FCSTD DOCUMENT  (FreeCAD 0.19R24276 (Git))
Label: pir-baffel-assembly
License: All rights reserved
LicenseURL: http://en.wikipedia.org/wiki/All_rights_reserved
objects: TechDraw::DrawViewDimension×10, App::Link×7, TechDraw::DrawViewAnnotation×5, TechDraw::DrawViewPart×4, App::DocumentObjectGroup×3, TechDraw::DrawHatch×3, PartDesign::CoordinateSystem×1, App::FeaturePython×1, App::Part×1, TechDraw::DrawSVGTemplate×1, TechDraw::DrawPage×1
note: 1 computed .brp shape members not serialized (recipe doc carries the construction recipe); baked Part::Feature solids carry a one-line shape summary decoded from their .brp
EXTERNAL_REF file=pir-baffel-top.FCStd obj=LCS_top
EXTERNAL_REF file=pir-baffel-top.FCStd obj=Body
EXTERNAL_REF file=pir-baffel-side.FCStd obj=LCS_side
EXTERNAL_REF file=pir-baffel-side.FCStd obj=Body
EXTERNAL_REF file=pir-baffel-bottomFront.FCStd obj=LCS_bottomFront
EXTERNAL_REF file=pir-baffel-bottomFront.FCStd obj=Body
EXTERNAL_REF file=pir-baffel-bottomBack.FCStd obj=LCS_bottomBack
EXTERNAL_REF file=pir-baffel-bottomBack.FCStd obj=Body
EXTERNAL_REF file=pir-baffel-screwBlock-assembly.FCStd obj=LCS_Origin
EXTERNAL_REF file=pir-baffel-screwBlock-assembly.FCStd obj=Model

FEATURE [App::DocumentObjectGroup] Parts
FEATURE [PartDesign::CoordinateSystem] LCS_Origin
  AttacherType = Attacher::AttachEngine3D
  MapMode = 2
  Support = -> [X_Axis]
FEATURE [App::DocumentObjectGroup] Constraints
FEATURE [App::FeaturePython] Variables  # WARN: FeaturePython — macro-defined, semantics opaque (R4)
FEATURE [App::Link] pir_baffel_top_Body
  AssemblyType = Asm4EE
  AttachedBy = #LCS_top
  AttachedTo = Parent Assembly#LCS_Origin
  LinkPlacement = pos=(0,0,-0.8) rot=(0,0,-1;1.5708rad)
  LinkedObject = -> <external pir-baffel-top.FCStd>#Body
  Placement = pos=(0,0,-0.8) rot=(0,0,-1;1.5708rad)
  expr: Placement = LCS_Origin.Placement * AttachmentOffset * pir_baffel_top#LCS_top.Placement ^ -1
FEATURE [App::Link] pir_baffel_side_left_Body
  AssemblyType = Asm4EE
  AttachedBy = #LCS_side
  AttachedTo = pir_baffel_top_Body#LCS_top
  AttachmentOffset = pos=(29,0,-26.6) rot=(0,1,0;4.71239rad)
  LinkPlacement = pos=(30.5785,9e-16,-25.8272) rot=(-0.576884,0.576884,0.578283;4.19019rad)
  LinkedObject = -> <external pir-baffel-side.FCStd>#Body
  Placement = pos=(30.5785,9e-16,-25.8272) rot=(-0.576884,0.576884,0.578283;4.19019rad)
  expr: Placement = pir_baffel_top_Body.Placement * pir_baffel_top#LCS_top.Placement * AttachmentOffset * pir_baffel_side#LCS_side.Placement ^ -1
FEATURE [App::Link] pir_baffel_side_right_Body
  AssemblyType = Asm4EE
  AttachedBy = #LCS_side
  AttachedTo = pir_baffel_top_Body#LCS_top
  AttachmentOffset = pos=(-29.1,0,-25) rot=(0,-1,0;4.71239rad)
  LinkPlacement = pos=(-30.6785,2e-16,-25.7728) rot=(0.577816,-0.577816,0.576418;4.18739rad)
  LinkedObject = -> <external pir-baffel-side.FCStd>#Body
  Placement = pos=(-30.6785,2e-16,-25.7728) rot=(0.577816,-0.577816,0.576418;4.18739rad)
  expr: Placement = pir_baffel_top_Body.Placement * pir_baffel_top#LCS_top.Placement * AttachmentOffset * pir_baffel_side#LCS_side.Placement ^ -1
FEATURE [App::Link] pir_baffel_bottomFront_Body
  AssemblyType = Asm4EE
  AttachedBy = #LCS_bottomFront
  AttachedTo = pir_baffel_top_Body#LCS_top
  AttachmentOffset = pos=(29,-30.7,-51.6) rot=(0.707107,0,0.707107;3.14159rad)
  LinkPlacement = pos=(7.1e-15,-30.7,-52.4) rot=(0,0,1;4.71239rad)
  LinkedObject = -> <external pir-baffel-bottomFront.FCStd>#Body
  Placement = pos=(7.1e-15,-30.7,-52.4) rot=(0,0,1;4.71239rad)
  expr: Placement = pir_baffel_top_Body.Placement * pir_baffel_top#LCS_top.Placement * AttachmentOffset * pir_baffel_bottomFront#LCS_bottomFront.Placement ^ -1
FEATURE [App::DocumentObjectGroup] Measures
FEATURE [App::Link] pir_baffel_bottomBack_Body
  AssemblyType = Asm4EE
  AttachedBy = #LCS_bottomBack
  AttachedTo = pir_baffel_top_Body#LCS_top
  AttachmentOffset = pos=(0,40,-54.1) rot=(0.707107,-0.707107,0;3.14159rad)
  LinkPlacement = pos=(-1e-16,40,-52.5) rot=(1,0,0;3.14159rad)
  LinkedObject = -> <external pir-baffel-bottomBack.FCStd>#Body
  Placement = pos=(-1e-16,40,-52.5) rot=(1,0,0;3.14159rad)
  expr: Placement = pir_baffel_top_Body.Placement * pir_baffel_top#LCS_top.Placement * AttachmentOffset * pir_baffel_bottomBack#LCS_bottomBack.Placement ^ -1
FEATURE [App::Link] pir_baffel_screwBlock1_assembly
  AssemblyType = Asm4EE
  AttachedBy = #LCS_Origin
  AttachedTo = pir_baffel_side_left_Body#LCS_side
  AttachmentOffset = pos=(-18.2,40,-4.8) rot=(0,0,1;0rad)
  LinkPlacement = pos=(33.8,40,-44.8) rot=(0,1,0;4.71239rad)
  LinkedObject = -> <external pir-baffel-screwBlock-assembly.FCStd>#Model
  Placement = pos=(33.8,40,-44.8) rot=(0,1,0;4.71239rad)
  expr: Placement = pir_baffel_side_left_Body.Placement * pir_baffel_side#LCS_side.Placement * AttachmentOffset * pir_baffel_screwBlock_assembly#LCS_Origin.Placement ^ -1
FEATURE [App::Link] pir_baffel_screwBlock2_assembly
  AssemblyType = Asm4EE
  AttachedBy = #LCS_Origin
  AttachedTo = pir_baffel_side_right_Body#LCS_side
  AttachmentOffset = pos=(20,39.8,-4.8) rot=(0,0,1;0rad)
  LinkPlacement = pos=(-33.9,39.8,-45) rot=(0,-1,0;4.71239rad)
  LinkedObject = -> <external pir-baffel-screwBlock-assembly.FCStd>#Model
  Placement = pos=(-33.9,39.8,-45) rot=(0,-1,0;4.71239rad)
  expr: Placement = pir_baffel_side_right_Body.Placement * pir_baffel_side#LCS_side.Placement * AttachmentOffset * pir_baffel_screwBlock_assembly#LCS_Origin.Placement ^ -1
FEATURE [App::Part] Model
  Configuration = 0
  Group = -> [LCS_Origin,Constraints,Variables,pir_baffel_top_Body,pir_baffel_side_left_Body,pir_baffel_side_right_Body,pir_baffel_bottomFront_Body,pir_baffel_bottomBack_Body,pir_baffel_screwBlock1_assembly,pir_baffel_screwBlock2_assembly]
  Origin = -> Origin
  Type = Assembly4 Model
FEATURE [TechDraw::DrawSVGTemplate] Template
  Height = 215.9
  Orientation = 1
  Width = 279.4
FEATURE [TechDraw::DrawViewPart] View
  CoarseView = false
  Direction = (0,0,1)
  Focus = 100
  HardHidden = false
  IsoCount = 0
  IsoHidden = false
  IsoVisible = false
  LockPosition = false
  Perspective = false
  Rotation = 0
  ScaleType = 0
  SeamHidden = false
  SeamVisible = true
  SmoothHidden = false
  SmoothVisible = true
  X = 83.0191
  XDirection = (0,-1,0)
  XSource = -> [pir_baffel_top_Body]
  Y = 177.335
FEATURE [TechDraw::DrawViewDimension] Dimension
  Arbitrary = false
  ArbitraryTolerances = false
  EqualTolerance = true
  FormatSpec = %.2f
  FormatSpecOverTolerance = %+.2f
  FormatSpecUnderTolerance = %+.2f
  Inverted = false
  LockPosition = false
  MeasureType = 1
  OverTolerance = 0
  References2D = -> [View]
  Rotation = 0
  ScaleType = 0
  TheoreticalExact = false
  Type = 2
  UnderTolerance = 0
  X = 60.7979
  Y = -2.1486
FEATURE [TechDraw::DrawViewDimension] Dimension001
  Arbitrary = false
  ArbitraryTolerances = false
  EqualTolerance = true
  FormatSpec = %.2f
  FormatSpecOverTolerance = %+.2f
  FormatSpecUnderTolerance = %+.2f
  Inverted = false
  LockPosition = false
  MeasureType = 1
  OverTolerance = 0
  References2D = -> [View]
  Rotation = 0
  ScaleType = 0
  TheoreticalExact = false
  Type = 1
  UnderTolerance = 0
  X = 0.678642
  Y = -33.0155
FEATURE [TechDraw::DrawViewAnnotation] Annotation
  Font = osifont
  LineSpace = 80
  LockPosition = false
  MaxWidth = -1
  Rotation = 0
  ScaleType = 0
  Text = Top
  TextSize = 5
  TextStyle = 0
  X = 83.114
  Y = 176.125
FEATURE [TechDraw::DrawViewPart] View001
  CoarseView = false
  Direction = (-1,0,0)
  Focus = 100
  HardHidden = false
  IsoCount = 0
  IsoHidden = false
  IsoVisible = false
  LockPosition = false
  Perspective = false
  Rotation = 0
  ScaleType = 0
  SeamHidden = false
  SeamVisible = true
  SmoothHidden = false
  SmoothVisible = true
  Source = -> [Model]
  X = 206.886
  XDirection = (0,-1,0)
  Y = 177.511
FEATURE [TechDraw::DrawViewDimension] Dimension002
  Arbitrary = false
  ArbitraryTolerances = false
  EqualTolerance = true
  FormatSpec = %.2f
  FormatSpecOverTolerance = %+.2f
  FormatSpecUnderTolerance = %+.2f
  Inverted = false
  LockPosition = false
  MeasureType = 1
  OverTolerance = 0
  References2D = -> [View001]
  Rotation = 0
  ScaleType = 0
  TheoreticalExact = false
  Type = 1
  UnderTolerance = 0
  X = -0.179257
  Y = 19.7555
FEATURE [TechDraw::DrawViewDimension] Dimension003
  Arbitrary = false
  ArbitraryTolerances = false
  EqualTolerance = true
  FormatSpec = %.2f
  FormatSpecOverTolerance = %+.2f
  FormatSpecUnderTolerance = %+.2f
  Inverted = false
  LockPosition = false
  MeasureType = 1
  OverTolerance = 0
  References2D = -> [View001]
  Rotation = 0
  ScaleType = 0
  TheoreticalExact = false
  Type = 2
  UnderTolerance = 0
  X = 60.557
  Y = 0.863629
FEATURE [TechDraw::DrawHatch] Hatch  label="HatchF0"
  HatchPattern = /snap/freecad/22/opt/local/FreeCAD-0.19/share/Mod/TechDraw/Patterns/simple.svg
  Source = -> View001 [Face0]
FEATURE [TechDraw::DrawViewAnnotation] Annotation001
  Font = osifont
  LineSpace = 80
  LockPosition = false
  MaxWidth = -1
  Rotation = 0
  ScaleType = 0
  Text = 2 X Side
  TextSize = 5
  TextStyle = 0
  X = 207.459
  Y = 180.011
FEATURE [TechDraw::DrawViewDimension] Dimension004
  Arbitrary = false
  ArbitraryTolerances = false
  EqualTolerance = true
  FormatSpec = %.2f
  FormatSpecOverTolerance = %+.2f
  FormatSpecUnderTolerance = %+.2f
  Inverted = false
  LockPosition = false
  MeasureType = 1
  OverTolerance = 0
  References2D = -> [View001]
  Rotation = 0
  ScaleType = 0
  TheoreticalExact = false
  Type = 1
  UnderTolerance = 0
  X = -40.5892
  Y = -2.10397
FEATURE [TechDraw::DrawViewDimension] Dimension005
  Arbitrary = false
  ArbitraryTolerances = false
  EqualTolerance = true
  FormatSpec = %.2f
  FormatSpecOverTolerance = %+.2f
  FormatSpecUnderTolerance = %+.2f
  Inverted = false
  LockPosition = false
  MeasureType = 1
  OverTolerance = 0
  References2D = -> [View001]
  Rotation = 0
  ScaleType = 0
  TheoreticalExact = false
  Type = 2
  UnderTolerance = 0
  X = -20.9332
  Y = -17.8111
FEATURE [TechDraw::DrawViewAnnotation] Annotation002
  Font = osifont
  LineSpace = 80
  LockPosition = false
  MaxWidth = -1
  Rotation = 0
  ScaleType = 0
  Text = 6 X Screw Block
  TextSize = 3
  TextStyle = 0
  X = 166.118
  Y = 157.388
FEATURE [TechDraw::DrawViewPart] View002
  CoarseView = false
  Direction = (0,0,-1)
  Focus = 100
  HardHidden = false
  IsoCount = 0
  IsoHidden = false
  IsoVisible = false
  LockPosition = false
  Perspective = false
  Rotation = 0
  ScaleType = 0
  SeamHidden = false
  SeamVisible = true
  SmoothHidden = false
  SmoothVisible = true
  Source = -> [Model]
  X = 87.1985
  XDirection = (0,-1,0)
  Y = 83.6659
FEATURE [TechDraw::DrawViewDimension] Dimension007
  Arbitrary = false
  ArbitraryTolerances = false
  EqualTolerance = true
  FormatSpec = %.2f
  FormatSpecOverTolerance = %+.2f
  FormatSpecUnderTolerance = %+.2f
  Inverted = false
  LockPosition = false
  MeasureType = 1
  OverTolerance = 0
  References2D = -> [View002]
  Rotation = 0
  ScaleType = 0
  TheoreticalExact = false
  Type = 1
  UnderTolerance = 0
  X = -40.2356
  Y = -37.5146
FEATURE [TechDraw::DrawViewDimension] Dimension009
  Arbitrary = false
  ArbitraryTolerances = false
  EqualTolerance = true
  FormatSpec = %.2f
  FormatSpecOverTolerance = %+.2f
  FormatSpecUnderTolerance = %+.2f
  Inverted = false
  LockPosition = false
  MeasureType = 1
  OverTolerance = 0
  References2D = -> [View002]
  Rotation = 0
  ScaleType = 0
  TheoreticalExact = false
  Type = 1
  UnderTolerance = 0
  X = 31.2834
  Y = -30.3899
FEATURE [TechDraw::DrawViewDimension] Dimension010
  Arbitrary = false
  ArbitraryTolerances = false
  EqualTolerance = true
  FormatSpec = %.2f
  FormatSpecOverTolerance = %+.2f
  FormatSpecUnderTolerance = %+.2f
  Inverted = false
  LockPosition = false
  MeasureType = 1
  OverTolerance = 0
  References2D = -> [View002]
  Rotation = 0
  ScaleType = 0
  TheoreticalExact = false
  Type = 2
  UnderTolerance = 0
  X = -63.2025
  Y = 2.15494
FEATURE [TechDraw::DrawViewDimension] Dimension011
  Arbitrary = false
  ArbitraryTolerances = false
  EqualTolerance = true
  FormatSpec = %.2f
  FormatSpecOverTolerance = %+.2f
  FormatSpecUnderTolerance = %+.2f
  Inverted = false
  LockPosition = false
  MeasureType = 0
  OverTolerance = 0
  References2D = -> [View002]
  References3D = -> [Model]
  Rotation = 0
  ScaleType = 0
  TheoreticalExact = false
  Type = 2
  UnderTolerance = 0
  X = 61.4866
  Y = 0.606588
FEATURE [TechDraw::DrawViewAnnotation] Annotation003
  Font = osifont
  LineSpace = 80
  LockPosition = false
  MaxWidth = -1
  Rotation = 0
  ScaleType = 0
  Text = Bottom Front
  TextSize = 5
  TextStyle = 0
  X = 116.34
  Y = 79.8901
FEATURE [TechDraw::DrawHatch] Hatch001  label="Hatch001F2"
  HatchPattern = /snap/freecad/22/opt/local/FreeCAD-0.19/share/Mod/TechDraw/Patterns/simple.svg
  Source = -> View002 [Face2]
FEATURE [TechDraw::DrawHatch] Hatch002  label="Hatch002F1"
  HatchPattern = /snap/freecad/22/opt/local/FreeCAD-0.19/share/Mod/TechDraw/Patterns/simple.svg
  Source = -> View002 [Face1]
FEATURE [TechDraw::DrawViewAnnotation] Annotation004
  Font = osifont
  LineSpace = 80
  LockPosition = false
  MaxWidth = -1
  Rotation = 0
  ScaleType = 0
  Text = Bottom Back
  TextSize = 5
  TextStyle = 0
  X = 46.0515
  Y = 78.7346
FEATURE [TechDraw::DrawViewPart] View003
  CoarseView = false
  Direction = (0.277,-0.903,0.327)
  Focus = 100
  HardHidden = false
  IsoCount = 0
  IsoHidden = false
  IsoVisible = false
  LockPosition = false
  Perspective = false
  Rotation = 0
  ScaleType = 0
  SeamHidden = false
  SeamVisible = true
  SmoothHidden = false
  SmoothVisible = true
  Source = -> [Model]
  X = 212.585
  XDirection = (0.918,0.35,0.187)
  Y = 79.7758
FEATURE [TechDraw::DrawPage] Page
  KeepUpdated = true
  NextBalloonIndex = 1
  ProjectionType = 0
  Template = -> Template
  Views = -> [View,Dimension,Dimension001,Annotation,View001,Dimension002,Dimension003,Annotation001,Dimension004,Dimension005,Annotation002,View002,Dimension007,Dimension009,Dimension010,Dimension011,Annotation003,Annotation004,View003]

RESOLVED EXTERNAL PARTS (link-assembly join: the EXTERNAL_REF files above that resolve inside this repo's crawl, each included once):
---- part pir-baffel-bottomBack.FCStd = doc fcstd_8937892381de ----
FCSTD DOCUMENT  (FreeCAD 0.19R24276 (Git))
Label: pir-baffel-bottomBack
License: All rights reserved
LicenseURL: http://en.wikipedia.org/wiki/All_rights_reserved
objects: Sketcher::SketchObject×1, PartDesign::Pad×1, PartDesign::CoordinateSystem×1, PartDesign::Body×1
note: 5 computed .brp shape members not serialized (recipe doc carries the construction recipe); baked Part::Feature solids carry a one-line shape summary decoded from their .brp

FEATURE [Sketcher::SketchObject] Sketch
  FullyConstrained = true
  MapMode = 5
  Support = -> [XY_Plane]
  sketch-geometry (4):
    g0: LineSegment StartX=-35.4 StartY=15 StartZ=0 EndX=35.4 EndY=15 EndZ=0
    g1: LineSegment StartX=35.4 StartY=15 StartZ=0 EndX=35.4 EndY=-15 EndZ=0
    g2: LineSegment StartX=35.4 StartY=-15 StartZ=0 EndX=-35.4 EndY=-15 EndZ=0
    g3: LineSegment StartX=-35.4 StartY=-15 StartZ=0 EndX=-35.4 EndY=15 EndZ=0
  constraints (10):
    c: Coincident(g0,g1)
    c: Coincident(g1,g2)
    c: Coincident(g2,g3)
    c: Coincident(g3,g0)
    c: Horizontal(g2)
    c: Vertical(g3)
    c: DistanceY(g3,g3) = 30
    c: DistanceX(g0,g0) = 70.8
    c: Symmetric(g0,g0,g-2)
    c: Symmetric(g0,g1,g-1)
FEATURE [PartDesign::Pad] Pad  label="BottomBack"
  Direction = (1,1,1)
  Length = 1.6
  Length2 = 100
  Profile = -> Sketch
  Type = 0
FEATURE [PartDesign::CoordinateSystem] LCS_bottomBack
  AttacherType = Attacher::AttachEngine3D
  MapMode = 45
  Placement = pos=(2e-16,3e-16,1.6) rot=(0,0,1;1.5708rad)
  Support = -> [Pad]
FEATURE [PartDesign::Body] Body
  Group = -> [Sketch,Pad,LCS_bottomBack]
  Origin = -> Origin
  Tip = -> Pad
---- part pir-baffel-bottomFront.FCStd = doc fcstd_61289e19d849 ----
FCSTD DOCUMENT  (FreeCAD 0.19R24276 (Git))
Label: pir-baffel-bottomFront
License: All rights reserved
LicenseURL: http://en.wikipedia.org/wiki/All_rights_reserved
objects: Sketcher::SketchObject×1, PartDesign::Pad×1, PartDesign::CoordinateSystem×1, PartDesign::Body×1
note: 5 computed .brp shape members not serialized (recipe doc carries the construction recipe); baked Part::Feature solids carry a one-line shape summary decoded from their .brp

FEATURE [Sketcher::SketchObject] Sketch
  FullyConstrained = true
  MapMode = 5
  Support = -> [XY_Plane]
  sketch-geometry (4):
    g0: LineSegment StartX=-24.25 StartY=29 StartZ=0 EndX=24.25 EndY=29 EndZ=0
    g1: LineSegment StartX=24.25 StartY=29 StartZ=0 EndX=24.25 EndY=-29 EndZ=0
    g2: LineSegment StartX=24.25 StartY=-29 StartZ=0 EndX=-24.25 EndY=-29 EndZ=0
    g3: LineSegment StartX=-24.25 StartY=-29 StartZ=0 EndX=-24.25 EndY=29 EndZ=0
  constraints (10):
    c: Coincident(g0,g1)
    c: Coincident(g1,g2)
    c: Coincident(g2,g3)
    c: Coincident(g3,g0)
    c: Horizontal(g2)
    c: Vertical(g3)
    c: DistanceY(g3,g3) = 58
    c: DistanceX(g0,g0) = 48.5
    c: Symmetric(g0,g0,g-2)
    c: Symmetric(g0,g1,g-1)
FEATURE [PartDesign::Pad] Pad  label="BottomFront"
  Direction = (1,1,1)
  Length = 1.6
  Length2 = 100
  Profile = -> Sketch
  Type = 0
FEATURE [PartDesign::CoordinateSystem] LCS_bottomFront
  AttacherType = Attacher::AttachEngine3D
  MapMode = 45
  Placement = pos=(1e-16,29,0.8) rot=(0.57735,0.57735,0.57735;4.18879rad)
  Support = -> [Pad]
FEATURE [PartDesign::Body] Body
  Group = -> [Sketch,Pad,LCS_bottomFront]
  Origin = -> Origin
  Tip = -> Pad
---- part pir-baffel-screwBlock-assembly.FCStd = doc fcstd_9de3331ebdb5 ----
FCSTD DOCUMENT  (FreeCAD 0.19R24276 (Git))
Label: pir-baffel-screwBlock-assembly
License: All rights reserved
LicenseURL: http://en.wikipedia.org/wiki/All_rights_reserved
objects: App::Link×3, App::DocumentObjectGroup×2, PartDesign::CoordinateSystem×1, App::FeaturePython×1, App::Part×1
note: 1 computed .brp shape members not serialized (recipe doc carries the construction recipe); baked Part::Feature solids carry a one-line shape summary decoded from their .brp
EXTERNAL_REF file=pir-baffel-screw-blocks.FCStd obj=LCS_screwBlock
EXTERNAL_REF file=pir-baffel-screw-blocks.FCStd obj=Body

FEATURE [App::DocumentObjectGroup] Parts
FEATURE [PartDesign::CoordinateSystem] LCS_Origin
  AttacherType = Attacher::AttachEngine3D
  MapMode = 2
  Support = -> [X_Axis]
FEATURE [App::DocumentObjectGroup] Constraints
FEATURE [App::FeaturePython] Variables  # WARN: FeaturePython — macro-defined, semantics opaque (R4)
FEATURE [App::Link] pir_baffel_screw_blocks_Body  label="pir_baffel_screw_block1_Body"
  AssemblyType = Asm4EE
  AttachedBy = #LCS_screwBlock
  AttachedTo = Parent Assembly#LCS_Origin
  LinkPlacement = pos=(-1e-16,2e-16,-1.6) rot=(0,0,-1;1.5708rad)
  LinkedObject = -> <external pir-baffel-screw-blocks.FCStd>#Body
  Placement = pos=(-1e-16,2e-16,-1.6) rot=(0,0,-1;1.5708rad)
  expr: Placement = LCS_Origin.Placement * AttachmentOffset * pir_baffel_screw_blocks#LCS_screwBlock.Placement ^ -1
FEATURE [App::Link] pir_baffel_screw_block2_Body
  AssemblyType = Asm4EE
  AttachedBy = #LCS_screwBlock
  AttachedTo = pir_baffel_screw_blocks_Body#LCS_screwBlock
  AttachmentOffset = pos=(0,0,1.6) rot=(0,0,1;0rad)
  LinkPlacement = pos=(-1e-16,2e-16,0) rot=(0,0,-1;1.5708rad)
  LinkedObject = -> <external pir-baffel-screw-blocks.FCStd>#Body
  Placement = pos=(-1e-16,2e-16,0) rot=(0,0,-1;1.5708rad)
  expr: Placement = pir_baffel_screw_blocks_Body.Placement * pir_baffel_screw_blocks#LCS_screwBlock.Placement * AttachmentOffset * pir_baffel_screw_blocks#LCS_screwBlock.Placement ^ -1
FEATURE [App::Link] pir_baffel_screw_block3_Body
  AssemblyType = Asm4EE
  AttachedBy = #LCS_screwBlock
  AttachedTo = pir_baffel_screw_block2_Body#LCS_screwBlock
  AttachmentOffset = pos=(0,0,1.6) rot=(0,0,1;0rad)
  LinkPlacement = pos=(-1e-16,2e-16,1.6) rot=(0,0,-1;1.5708rad)
  LinkedObject = -> <external pir-baffel-screw-blocks.FCStd>#Body
  Placement = pos=(-1e-16,2e-16,1.6) rot=(0,0,-1;1.5708rad)
  expr: Placement = pir_baffel_screw_block2_Body.Placement * pir_baffel_screw_blocks#LCS_screwBlock.Placement * AttachmentOffset * pir_baffel_screw_blocks#LCS_screwBlock.Placement ^ -1
FEATURE [App::Part] Model
  Configuration = 0
  Group = -> [LCS_Origin,Constraints,Variables,pir_baffel_screw_blocks_Body,pir_baffel_screw_block2_Body,pir_baffel_screw_block3_Body]
  Origin = -> Origin
  Type = Assembly4 Model
---- part pir-baffel-side.FCStd = doc fcstd_616bb7e95e97 ----
FCSTD DOCUMENT  (FreeCAD 0.19R24276 (Git))
Label: pir-baffel-side
License: All rights reserved
LicenseURL: http://en.wikipedia.org/wiki/All_rights_reserved
objects: Sketcher::SketchObject×1, PartDesign::Pad×1, PartDesign::CoordinateSystem×1, PartDesign::Body×1
note: 5 computed .brp shape members not serialized (recipe doc carries the construction recipe); baked Part::Feature solids carry a one-line shape summary decoded from their .brp

FEATURE [Sketcher::SketchObject] Sketch
  FullyConstrained = true
  MapMode = 5
  Support = -> [XY_Plane]
  sketch-geometry (4):
    g0: LineSegment StartX=-55 StartY=26.6 StartZ=0 EndX=55 EndY=26.6 EndZ=0
    g1: LineSegment StartX=55 StartY=26.6 StartZ=0 EndX=55 EndY=-26.6 EndZ=0
    g2: LineSegment StartX=55 StartY=-26.6 StartZ=0 EndX=-55 EndY=-26.6 EndZ=0
    g3: LineSegment StartX=-55 StartY=-26.6 StartZ=0 EndX=-55 EndY=26.6 EndZ=0
  constraints (10):
    c: Coincident(g0,g1)
    c: Coincident(g1,g2)
    c: Coincident(g2,g3)
    c: Coincident(g3,g0)
    c: Horizontal(g2)
    c: Vertical(g1)
    c: DistanceY(g3,g3) = 53.2
    c: DistanceX(g0,g0) = 110
    c: Symmetric(g0,g0,g-2)
    c: Symmetric(g0,g2,g-1)
FEATURE [PartDesign::Pad] Pad  label="Side"
  Direction = (1,1,1)
  Length = 1.6
  Length2 = 100
  Profile = -> Sketch
  Type = 0
FEATURE [PartDesign::CoordinateSystem] LCS_side
  AttacherType = Attacher::AttachEngine3D
  MapMode = 45
  Placement = pos=(7e-16,-0.776642,1.57664) rot=(0.001211,-0.001211,0.999999;1.5708rad)
  Support = -> [Pad]
FEATURE [PartDesign::Body] Body
  Group = -> [Sketch,Pad,LCS_side]
  Origin = -> Origin
  Tip = -> Pad
---- part pir-baffel-top.FCStd = doc fcstd_5bcb7b59a8eb ----
FCSTD DOCUMENT  (FreeCAD 0.19R24276 (Git))
Label: pir-baffel-top
License: All rights reserved
LicenseURL: http://en.wikipedia.org/wiki/All_rights_reserved
objects: Sketcher::SketchObject×1, PartDesign::Pad×1, PartDesign::CoordinateSystem×1, PartDesign::Body×1
note: 5 computed .brp shape members not serialized (recipe doc carries the construction recipe); baked Part::Feature solids carry a one-line shape summary decoded from their .brp

FEATURE [Sketcher::SketchObject] Sketch
  FullyConstrained = true
  MapMode = 5
  Support = -> [XY_Plane]
  sketch-geometry (4):
    g0: LineSegment StartX=-55 StartY=29 StartZ=0 EndX=55 EndY=29 EndZ=0
    g1: LineSegment StartX=55 StartY=29 StartZ=0 EndX=55 EndY=-29 EndZ=0
    g2: LineSegment StartX=55 StartY=-29 StartZ=0 EndX=-55 EndY=-29 EndZ=0
    g3: LineSegment StartX=-55 StartY=-29 StartZ=0 EndX=-55 EndY=29 EndZ=0
  constraints (10):
    c: Coincident(g0,g1)
    c: Coincident(g1,g2)
    c: Coincident(g2,g3)
    c: Coincident(g3,g0)
    c: Horizontal(g2)
    c: Vertical(g1)
    c: DistanceX(g0,g0) = 110
    c: DistanceY(g3,g3) = 58
    c: Symmetric(g0,g0,g-2)
    c: Symmetric(g0,g2,g-1)
FEATURE [PartDesign::Pad] Pad
  Direction = (1,1,1)
  Length = 1.6
  Length2 = 100
  Profile = -> Sketch
  Type = 0
FEATURE [PartDesign::CoordinateSystem] LCS_top
  AttacherType = Attacher::AttachEngine3D
  MapMode = 45
  Placement = pos=(0,0,0.8) rot=(0,0,1;1.5708rad)
  Support = -> [Pad]
FEATURE [PartDesign::Body] Body
  Group = -> [Sketch,Pad,LCS_top]
  Origin = -> Origin
  Tip = -> Pad
